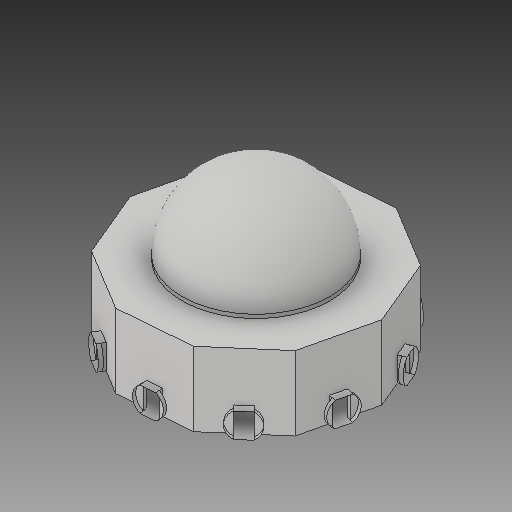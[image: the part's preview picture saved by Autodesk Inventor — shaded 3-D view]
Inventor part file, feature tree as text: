
AUTODESK INVENTOR PART (.ipt)
format: ipt  version: 2017 (Build 210142000, 142)  size: 339,456 bytes
history: native  units: in
note: dims shown in document units (in); Inventor stores cm internally (conversion verified against a paired STEP export)
features: extrude x5, sketch x5, other x2, pattern_circular x1, delete_face x1
ambient origin geometry x8: Origin, YZ Plane, XZ Plane, XY Plane, X Axis, Y Axis, Z Axis, Center Point
bodies: Solid1 (feature_tree)
feature tree (14):
  extrude  "bace"  Depth=1.0in TaperAngle=0.0deg
  extrude  "bace wall"  Depth=20.0in TaperAngle=0.0deg
  extrude  "bace cieiling"  Depth=6.6667in
  other  "dome work plane"
  other  "dome"
  extrude  "door frame"  Depth=1.0in
  extrude  "corridor connect"  Depth=21.0in
  pattern_circular  "Circular Pattern1"  Angle=90.0deg  [1 undecoded]
  delete_face  "Delete Face2"
  sketch  "Sketch1"  dims[d0=62.0in d1=1.0in d2=0.0in]
  sketch  "Sketch2"  dims[d4=1.0in d5=20.0in d6=0.0in]
  sketch  "Sketch3"  dims[d8=1.0in d9=0.0in d16=2.0in d17=6.6667in]
  sketch  "Sketch8"  dims[d18=1.0in d19=0.0in d28=40.0in]
  sketch  "Sketch10"  dims[d32=20.0in d33=21.0in d34=90.0deg d35=3.937in d36=360.0deg d74=4.0in d76=3.8873in d77=3.8873in d81=1.6458in d86=3.3333in d87=1.0in d90=1.0in d91=1.0in d92=0.0in]
note: 1 required parameter value undecoded (feature->parameter linkage not recoverable at this tier; creation-order binding heuristic only, values carry confidence <= 0.55)
